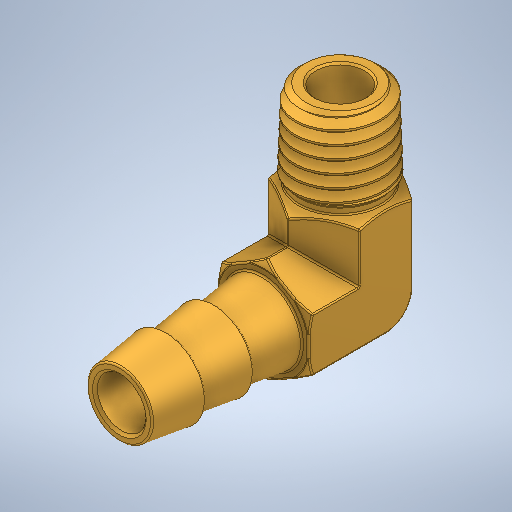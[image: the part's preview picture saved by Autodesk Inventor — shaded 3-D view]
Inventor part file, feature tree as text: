
AUTODESK INVENTOR PART (.ipt)
format: ipt  version: 2025 (Build 290162000, 162)  size: 774,144 bytes
history: native  units: mm
features: fillet x1
ambient origin geometry x8: Origin, YZ Plane, XZ Plane, XY Plane, X Axis, Y Axis, Z Axis, Center Point
bodies: Solid1 (feature_tree)
feature tree (1):
  fillet  "Fillet6"  [1 undecoded]
note: 1 required parameter value undecoded (feature->parameter linkage not recoverable at this tier; creation-order binding heuristic only, values carry confidence <= 0.55)
